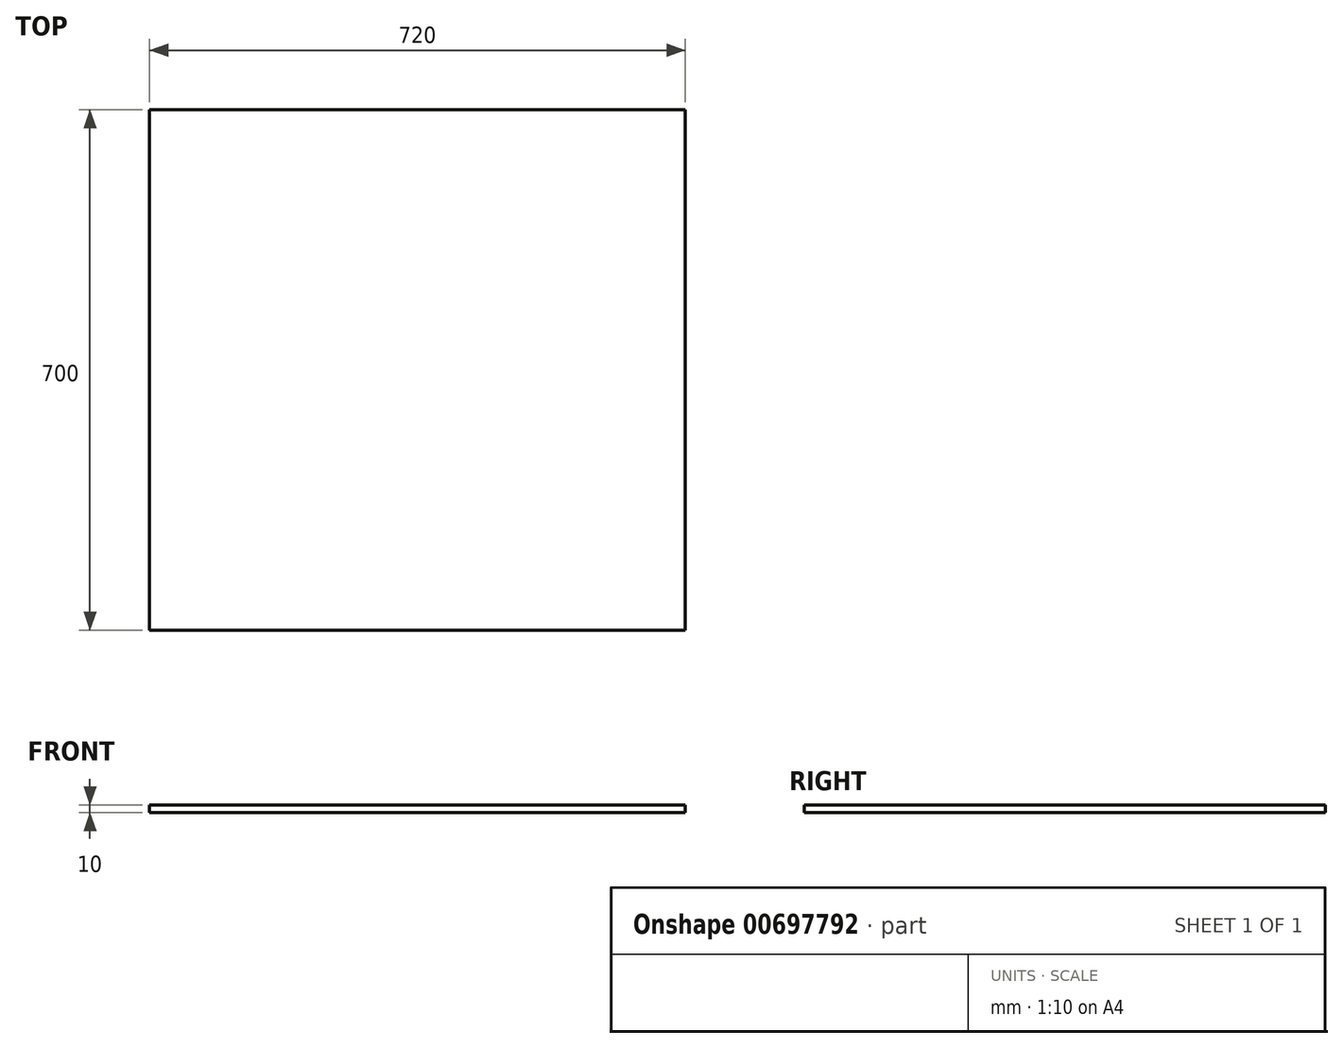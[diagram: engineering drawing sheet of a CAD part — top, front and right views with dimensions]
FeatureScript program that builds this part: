
annotation { "Feature Type Name" : "Feature", "Feature Type Description" : "" }
export const myFeature = defineFeature(function(context is Context, id is Id, definition is map)
    precondition{}
    {
        {
            var Q0;
            Q0=qCreatedBy(makeId("Top.planeOp"),FACE);
            var sketch = newSketch(context, id + "F0", { "sketchPlane" : qUnion([Q0])});
            skLineSegment(sketch, "E0.bottom", {"start": v(-577.16, 606.15) * mm, "end": v(142.84, 606.15) * mm});
            skLineSegment(sketch, "E0.top", {"start": v(-577.16, -93.85) * mm, "end": v(142.84, -93.85) * mm});
            skLineSegment(sketch, "E0.left", {"start": v(-577.16, 606.15) * mm, "end": v(-577.16, -93.85) * mm});
            skLineSegment(sketch, "E0.right", {"start": v(142.84, 606.15) * mm, "end": v(142.84, -93.85) * mm});
            skSolve(sketch);
        }
        {
            var Q0;
            Q0 = qSketchRegion(id + "F0", true);
            extrude(context, id + "F1", {"entities" : qUnion([Q0]), "depth" : 10 * mm, "offsetDistance" : 25 * mm});
        }
    });
